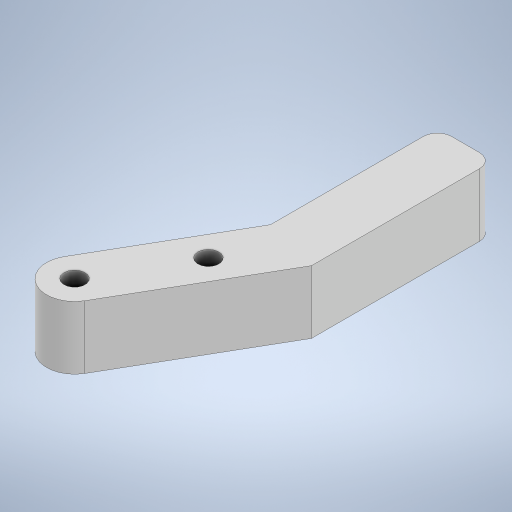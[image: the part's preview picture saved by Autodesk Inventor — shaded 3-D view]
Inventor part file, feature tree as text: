
AUTODESK INVENTOR PART (.ipt)
format: ipt  version: 2023 (Build 270158000, 158)  size: 255,488 bytes
history: native  units: mm
features: other x1, extrude x1, sketch x1
ambient origin geometry x8: Origin, YZ Plane, XZ Plane, XY Plane, X Axis, Y Axis, Z Axis, Center Point
bodies: Body1 (feature_tree)
feature tree (3):
  other  "Sólido1"
  extrude  "Extrusión1"  Depth=26.0mm
  sketch  "Boceto1"  dims[d0=90.0deg d2=26.0mm d7=8.0mm d10=150.0deg d11=8.0mm d12=5.0mm d13=4.0mm d14=4.0mm d15=2.0mm d16=3.0mm d17=3.0mm d18=14.0mm d19=48.0mm d20=9.0mm d21=0.0mm]
